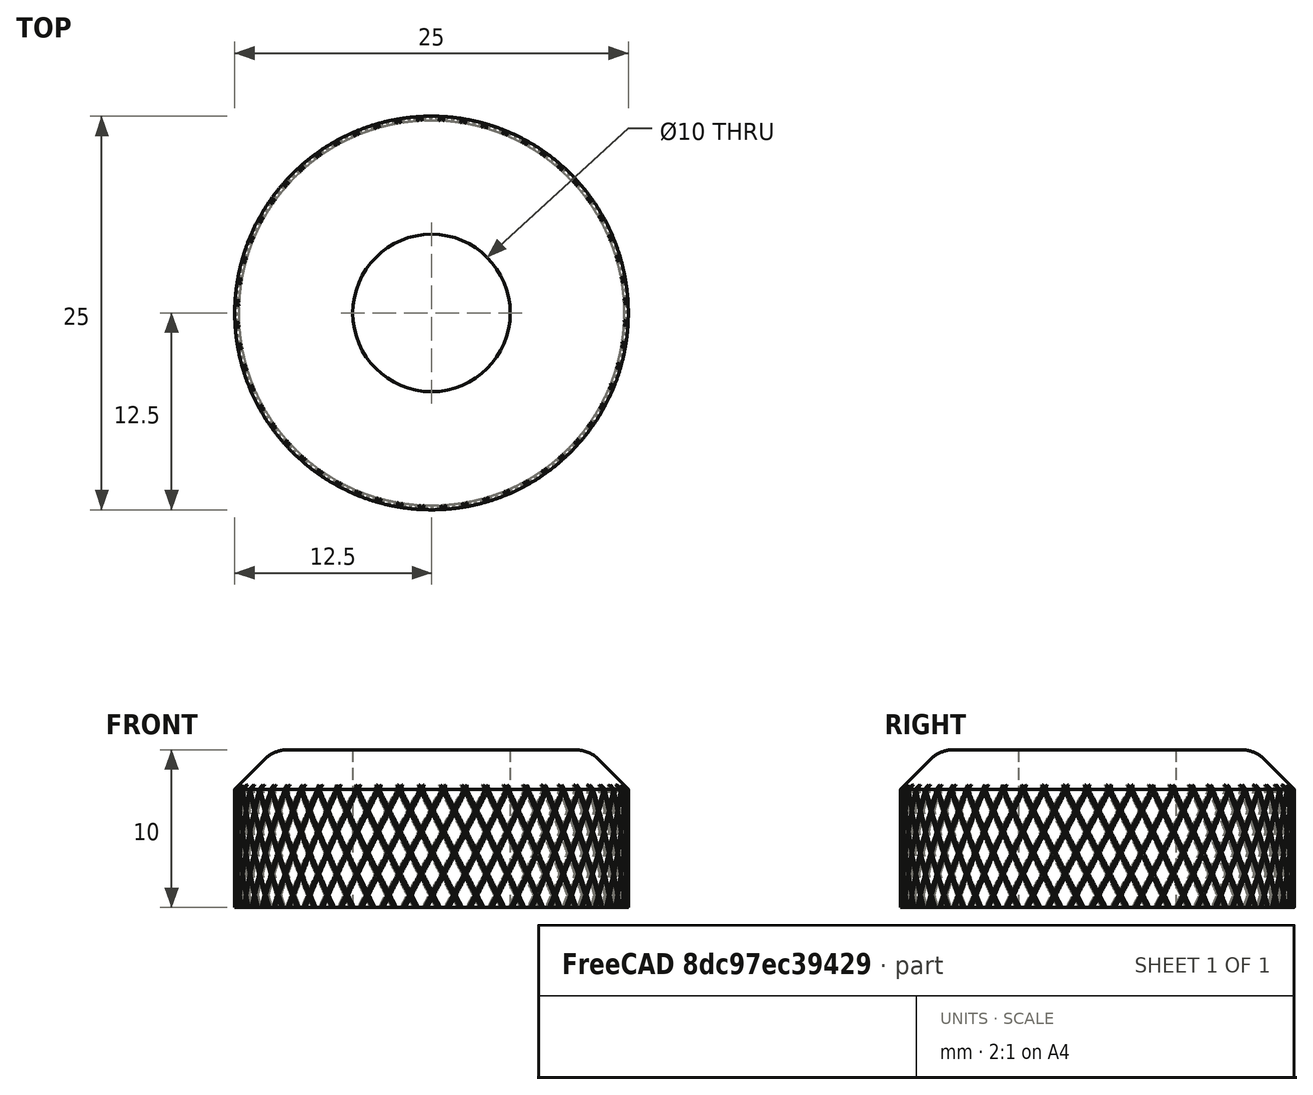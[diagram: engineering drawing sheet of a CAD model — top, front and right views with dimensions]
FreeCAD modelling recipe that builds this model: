
FCSTD DOCUMENT  (FreeCAD 1.0R39319 (Git))
Label: KnurlingModel
License: All rights reserved
LicenseURL: https://en.wikipedia.org/wiki/All_rights_reserved
objects: TechDraw::DrawViewDimension×9, Sketcher::SketchObject×3, TechDraw::DrawProjGroupItem×3, PartDesign::SubtractiveHelix×2, TechDraw::DrawViewAnnotation×2, PartDesign::Pad×1, PartDesign::Chamfer×1, PartDesign::Hole×1, PartDesign::Fillet×1, PartDesign::PolarPattern×1, PartDesign::Body×1, TechDraw::DrawSVGTemplate×1, TechDraw::DrawViewImage×1, TechDraw::DrawProjGroup×1, TechDraw::DrawViewSection×1, TechDraw::DrawPage×1
note: 38 computed .brp shape members not serialized (recipe doc carries the construction recipe); baked Part::Feature solids carry a one-line shape summary decoded from their .brp

FEATURE [Sketcher::SketchObject] Sketch
  ArcFitTolerance = 1e-06
  AttachmentSupport = -> [XY_Plane]
  FullyConstrained = true
  MakeInternals = false
  MapMode = 5
  sketch-geometry (1):
    g0: Circle CenterX=0 CenterY=0 CenterZ=0 NormalX=0 NormalY=0 NormalZ=1 AngleXU=0 Radius=12.5
  constraints (2):
    c: Diameter(g0) = 25
    c: Coincident(g0,g-1)
FEATURE [PartDesign::Pad] Pad
  Direction = (0,0,1)
  Length = 10
  Length2 = 10
  Profile = -> Sketch
  ReferenceAxis = -> Sketch [N_Axis]
  Refine = true
  Suppressed = false
  Type = 0
FEATURE [PartDesign::Chamfer] Chamfer
  Angle = 45
  Base = -> Pad [Edge3]
  BaseFeature = -> Pad
  ChamferType = 0
  FlipDirection = false
  Refine = true
  Size = 2.5
  Size2 = 1
  SupportTransform = false
  Suppressed = false
  UseAllEdges = false
FEATURE [Sketcher::SketchObject] Sketch001
  ArcFitTolerance = 1e-06
  AttachmentOffset = pos=(0,0,-2) rot=(0,0,1;0rad)
  AttachmentSupport = -> [XY_Plane]
  FullyConstrained = true
  MakeInternals = false
  MapMode = 5
  Placement = pos=(0,0,-2) rot=(0,0,1;0rad)
  sketch-geometry (3):
    g0: LineSegment StartX=-0.724874 StartY=13.9812 StartZ=0 EndX=0 EndY=12.2312 EndZ=0
    g1: LineSegment StartX=0 StartY=12.2312 StartZ=0 EndX=0.724874 EndY=13.9812 EndZ=0
    g2: ArcOfCircle CenterX=0 CenterY=0 CenterZ=0 NormalX=0 NormalY=0 NormalZ=1 AngleXU=0 Radius=14 StartAngle=1.519 EndAngle=1.6226
  constraints (9):
    c: PointOnObject(g0,g-2)
    c: Coincident(g0,g1)
    c: Angle(g1,g0) = 0.785398
    c: Coincident(g2,g-1)
    c: Coincident(g2,g1)
    c: Coincident(g2,g0)
    c: Radius(g2) = 14
    c: Horizontal(g1,g0)
    c: DistanceY(g1,g1) = 1.75
FEATURE [Sketcher::SketchObject] MirroredSketch
  ArcFitTolerance = 1e-06
  FullyConstrained = true
  MakeInternals = false
  Placement = pos=(0,0,-2) rot=(0,0,1;0.120951rad)
  sketch-geometry (3):
    g0: LineSegment StartX=-0.724874 StartY=-13.9812 StartZ=0 EndX=0 EndY=-12.2312 EndZ=0
    g1: LineSegment StartX=0 StartY=-12.2312 StartZ=0 EndX=0.724874 EndY=-13.9812 EndZ=0
    g2: ArcOfCircle CenterX=0 CenterY=0 CenterZ=0 NormalX=0 NormalY=0 NormalZ=1 AngleXU=0 Radius=14 StartAngle=4.66059 EndAngle=4.76419
  constraints (9):
    c: Coincident(g0,g1)
    c: Angle(g1,g0) = -0.785398
    c: Coincident(g2,g1)
    c: Coincident(g2,g0)
    c: Radius(g2) = 14
    c: PointOnObject(g0,g-2)
    c: Horizontal(g1,g0)
    c: DistanceY(g1,g1) = 1.75
    c: Coincident(g2,g-1)
FEATURE [PartDesign::Hole] Hole
  BaseFeature = -> Chamfer
  CustomThreadClearance = 0
  Depth = 25
  DepthType = 0
  Diameter = 10
  DrillForDepth = false
  DrillPoint = 1
  DrillPointAngle = 118
  HoleCutCountersinkAngle = 90
  HoleCutCustomValues = false
  HoleCutDepth = 0
  HoleCutDiameter = 6.1
  HoleCutType = 0
  ModelThread = false
  Profile = -> Chamfer [Face4]
  Refine = true
  Suppressed = false
  Tapered = false
  TaperedAngle = 90
  ThreadClass = 0
  ThreadDepth = 25
  ThreadDepthType = 0
  ThreadDirection = 0
  ThreadFit = 0
  ThreadSize = 0
  ThreadType = 0
  Threaded = false
  UseCustomThreadClearance = false
FEATURE [PartDesign::Fillet] Fillet
  Base = -> Hole [Edge5]
  BaseFeature = -> Hole
  Radius = 2
  Refine = true
  SupportTransform = false
  Suppressed = false
  UseAllEdges = false
FEATURE [PartDesign::SubtractiveHelix] SubtractiveHelix
  Angle = 0
  Axis = (1e-16,1e-16,1)
  Base = (0,0,0)
  BaseFeature = -> Fillet
  Growth = 0
  HasBeenEdited = true
  Height = 12
  LeftHanded = false
  Mode = 0
  Outside = false
  Pitch = 150
  Profile = -> Sketch001
  ReferenceAxis = -> Z_Axis
  Refine = true
  Suppressed = false
  Tolerance = 0.1
  Turns = 0.08
FEATURE [PartDesign::SubtractiveHelix] SubtractiveHelix001
  Angle = 0
  Axis = (1e-16,1e-16,1)
  Base = (0,0,0)
  BaseFeature = -> SubtractiveHelix
  Growth = 0
  HasBeenEdited = true
  Height = 12
  LeftHanded = true
  Mode = 0
  Outside = false
  Pitch = 150
  Profile = -> MirroredSketch
  ReferenceAxis = -> Z_Axis
  Refine = true
  Suppressed = false
  Tolerance = 0.1
  Turns = 0.08
FEATURE [PartDesign::PolarPattern] PolarPattern
  Angle = 360
  Axis = -> Sketch001 [N_Axis]
  BaseFeature = -> SubtractiveHelix001
  Mode = 0
  Occurrences = 56
  Offset = 120
  Originals = -> [SubtractiveHelix,SubtractiveHelix001]
  Refine = true
  Suppressed = false
  TransformMode = 0
FEATURE [PartDesign::Body] Body
  AllowCompound = false
  Group = -> [Sketch,Pad,Chamfer,Sketch001,MirroredSketch,Hole,Fillet,SubtractiveHelix,SubtractiveHelix001,PolarPattern]
  Origin = -> Origin
  Tip = -> PolarPattern
FEATURE [TechDraw::DrawSVGTemplate] Template
  EditableTexts = approval_person=B. Hecate; creator=KUN-YI CHEN; date_of_issue=10/25/25; document_type=Component Drawing; general_tolerances=ISO 2768-m; identification_number=DN; language_code=EN; legal_owner_1=UWINGS TECHNOLOIGES; part_material=Stainless steel Mat.No. 1.4301; revision_index=AAA; scale=1 : 1; sheet_number=1 / 1; title=Knurling Demo Model
  Height = 210
  Orientation = 1
  Template = <path>
  Width = 297
FEATURE [TechDraw::DrawViewImage] ActiveView
  Height = 72.4
  ImageFile = <userpath>/.cache/FreeCAD/Cache/FreeCAD_Doc_d9a276a7-9c46-4152-82e7-83487e9de5cd_6feaea_92105/PageActiveViewvjlq21.png
  LockPosition = false
  Rotation = 0
  Scale = 0.8
  ScaleType = 2
  Width = 72
  X = 165.05
  Y = 154.756
FEATURE [TechDraw::DrawProjGroupItem] View  label="Front"
  CoarseView = false
  Direction = (6e-16,-2e-16,-1)
  Focus = 150
  HardHidden = false
  IsoCount = 0
  IsoHidden = false
  IsoVisible = false
  LockPosition = true
  Perspective = false
  Rotation = 0
  RotationVector = (1,0,0)
  Scale = 2.66667
  ScaleType = 2
  ScrubCount = 0
  SeamHidden = false
  SeamVisible = false
  SmoothHidden = false
  SmoothVisible = true
  Source = -> [Fillet]
  Type = 0
  X = 0
  XDirection = (-1e-16,1,-2e-16)
  Y = 0
FEATURE [TechDraw::DrawProjGroupItem] ProjItem  label="Top"
  CoarseView = false
  Direction = (1,1e-16,6e-16)
  Focus = 100
  HardHidden = false
  IsoCount = 0
  IsoHidden = false
  IsoVisible = false
  LockPosition = false
  Perspective = false
  Rotation = 0
  RotationVector = (1,0,0)
  Scale = 2.66667
  ScaleType = 2
  ScrubCount = 1
  SeamHidden = false
  SeamVisible = false
  SmoothHidden = false
  SmoothVisible = true
  Source = -> [Fillet]
  Type = 4
  X = 0
  XDirection = (-1e-16,1,-2e-16)
  Y = -71.6667
FEATURE [TechDraw::DrawProjGroup] ProjGroup
  Anchor = -> View
  AutoDistribute = true
  LockPosition = false
  ProjectionType = 0
  Rotation = 0
  Scale = 2.66667
  ScaleType = 2
  Source = -> [Fillet]
  Views = -> [View,ProjItem]
  X = 74.1881
  Y = 154.756
  spacingX = 25
  spacingY = 25
FEATURE [TechDraw::DrawViewDimension] Dimension
  AngleOverride = false
  Arbitrary = false
  ArbitraryTolerances = false
  BoxCorners = (2) [(-33.3333,-33.3333,0),(33.3333,33.3333,0)]
  EqualTolerance = true
  ExtensionAngle = 0
  FormatSpec = ⌀%.2w
  FormatSpecOverTolerance = %+.2w
  FormatSpecUnderTolerance = %+.2w
  Inverted = false
  LineAngle = 0
  LockPosition = false
  MeasureType = 1
  OverTolerance = 0
  References2D = -> [View]
  Rotation = 0
  ScaleType = 0
  TheoreticalExact = false
  Type = 5
  UnderTolerance = 0
  X = 39.1122
  Y = -24.381
FEATURE [TechDraw::DrawViewSection] SectionView  label="Section A-A"
  BaseView = -> View
  CoarseView = false
  CutSurfaceDisplay = 2
  Direction = (1,4e-16,6e-16)
  FileGeomPattern = <path>
  FileHatchPattern = <path>
  Focus = 100
  FuseBeforeCut = false
  HardHidden = false
  HatchOffset = (0,0,0)
  HatchRotation = 0
  HatchScale = 1
  IsoCount = 0
  IsoHidden = false
  IsoVisible = false
  LockPosition = false
  NameGeomPattern = Diamond
  Perspective = false
  Rotation = 0
  Scale = 2.66667
  ScaleType = 2
  ScrubCount = 1
  SeamHidden = false
  SeamVisible = false
  SectionDirection = 4
  SectionLineStretch = 1
  SectionNormal = (1,4e-16,6e-16)
  SectionOrigin = (0,0,5)
  SectionSymbol = A
  SmoothHidden = false
  SmoothVisible = true
  Source = -> [Fillet]
  TrimAfterCut = false
  UsePreviousCut = false
  X = 68.9616
  XDirection = (-4e-16,1,-2e-16)
  Y = 76.6489
FEATURE [TechDraw::DrawViewDimension] Dimension001
  AngleOverride = false
  Arbitrary = false
  ArbitraryTolerances = false
  BoxCorners = (2) [(-33.3333,-13.3333,-1e-07),(33.3333,13.3333,1e-07)]
  EqualTolerance = true
  ExtensionAngle = 0
  FormatSpec = %.2w
  FormatSpecOverTolerance = %+.2w
  FormatSpecUnderTolerance = %+.2w
  Inverted = false
  LineAngle = 0
  LockPosition = false
  MeasureType = 1
  OverTolerance = 0
  References2D = -> [SectionView]
  Rotation = 0
  ScaleType = 0
  TheoreticalExact = false
  Type = 1
  UnderTolerance = 0
  X = 0
  Y = -32.2529
FEATURE [TechDraw::DrawViewDimension] Dimension002
  AngleOverride = false
  Arbitrary = false
  ArbitraryTolerances = false
  BoxCorners = (2) [(-33.3333,-13.3333,-1e-07),(33.3333,13.3333,1e-07)]
  EqualTolerance = true
  ExtensionAngle = 0
  FormatSpec = R%.2w
  FormatSpecOverTolerance = %+.2w
  FormatSpecUnderTolerance = %+.2w
  Inverted = false
  LineAngle = 0
  LockPosition = false
  MeasureType = 1
  OverTolerance = 0
  References2D = -> [SectionView]
  Rotation = 0
  ScaleType = 0
  TheoreticalExact = false
  Type = 4
  UnderTolerance = 0
  X = 27.6489
  Y = 28.5213
FEATURE [TechDraw::DrawViewDimension] Dimension003
  AngleOverride = false
  Arbitrary = false
  ArbitraryTolerances = false
  BoxCorners = (2) [(-33.3333,-13.3333,-1e-07),(33.3333,13.3333,1e-07)]
  EqualTolerance = true
  ExtensionAngle = 0
  FormatSpec = %.2w
  FormatSpecOverTolerance = %+.2w
  FormatSpecUnderTolerance = %+.2w
  Inverted = false
  LineAngle = 0
  LockPosition = false
  MeasureType = 1
  OverTolerance = 0
  References2D = -> [SectionView]
  Rotation = 0
  ScaleType = 0
  TheoreticalExact = false
  Type = 2
  UnderTolerance = 0
  X = 65.6013
  Y = -4.1905
FEATURE [TechDraw::DrawViewDimension] Dimension004
  AngleOverride = false
  Arbitrary = false
  ArbitraryTolerances = false
  BoxCorners = (2) [(-33.3333,-13.3333,-1e-07),(33.3333,13.3333,1e-07)]
  EqualTolerance = true
  ExtensionAngle = 0
  FormatSpec = %.2w
  FormatSpecOverTolerance = %+.2w
  FormatSpecUnderTolerance = %+.2w
  Inverted = false
  LineAngle = 0
  LockPosition = false
  MeasureType = 1
  OverTolerance = 0
  References2D = -> [SectionView]
  Rotation = 0
  ScaleType = 0
  TheoreticalExact = false
  Type = 6
  UnderTolerance = 0
  X = -0.336242
  Y = 28.4378
FEATURE [TechDraw::DrawViewDimension] Dimension005
  AngleOverride = false
  Arbitrary = false
  ArbitraryTolerances = false
  BoxCorners = (2) [(-33.3333,-13.3333,-1e-07),(33.3333,13.3333,1e-07)]
  EqualTolerance = true
  ExtensionAngle = 0
  FormatSpec = %.2w
  FormatSpecOverTolerance = %+.2w
  FormatSpecUnderTolerance = %+.2w
  Inverted = false
  LineAngle = 0
  LockPosition = false
  MeasureType = 1
  OverTolerance = 0
  References2D = -> [SectionView]
  Rotation = 0
  ScaleType = 0
  TheoreticalExact = false
  Type = 2
  UnderTolerance = 0
  X = 48.3444
  Y = -7.55789
FEATURE [TechDraw::DrawViewAnnotation] Annotation
  Font = osifont
  LineSpace = 100
  LockPosition = false
  MaxWidth = -1
  Rotation = 0
  ScaleType = 0
  Text = Knurling/Helix | Pitch: 150 | Height:12
  TextSize = 5
  TextStyle = 0
  X = 241.672
  Y = 160.061
FEATURE [TechDraw::DrawProjGroupItem] View001
  CoarseView = false
  Direction = (0,0,1)
  Focus = 100
  HardHidden = false
  IsoCount = 0
  IsoHidden = false
  IsoVisible = false
  LockPosition = false
  Perspective = false
  Rotation = 0
  RotationVector = (1,0,0)
  Scale = 5
  ScaleType = 2
  ScrubCount = 1
  SeamHidden = false
  SeamVisible = false
  SmoothHidden = false
  SmoothVisible = true
  Source = -> [Sketch001]
  Type = 0
  X = 218.42
  XDirection = (1,0,0)
  Y = 113.229
FEATURE [TechDraw::DrawViewDimension] Dimension006
  AngleOverride = false
  Arbitrary = false
  ArbitraryTolerances = false
  BoxCorners = (2) [(-3.62437,-4.42195,0),(3.62437,4.42195,0)]
  EqualTolerance = true
  ExtensionAngle = 0
  FormatSpec = R%.2w
  FormatSpecOverTolerance = %+.2w
  FormatSpecUnderTolerance = %+.2w
  Inverted = false
  LineAngle = 0
  LockPosition = false
  MeasureType = 1
  OverTolerance = 0
  References2D = -> [View001]
  Rotation = 0
  ScaleType = 0
  TheoreticalExact = false
  Type = 4
  UnderTolerance = 0
  X = 39.7177
  Y = -17.8998
FEATURE [TechDraw::DrawViewDimension] Dimension007
  AngleOverride = false
  Arbitrary = false
  ArbitraryTolerances = false
  BoxCorners = (2) [(-3.62437,-4.42195,0),(3.62437,4.42195,0)]
  EqualTolerance = true
  ExtensionAngle = 0
  FormatSpec = %.2w
  FormatSpecOverTolerance = %+.2w
  FormatSpecUnderTolerance = %+.2w
  Inverted = false
  LineAngle = 0
  LockPosition = false
  MeasureType = 1
  OverTolerance = 0
  References2D = -> [View001]
  Rotation = 0
  ScaleType = 0
  TheoreticalExact = false
  Type = 6
  UnderTolerance = 0
  X = -2.19548
  Y = 19.6146
FEATURE [TechDraw::DrawViewDimension] Dimension008
  AngleOverride = false
  Arbitrary = false
  ArbitraryTolerances = false
  BoxCorners = (2) [(-3.62437,-4.42195,0),(3.62437,4.42195,0)]
  EqualTolerance = true
  ExtensionAngle = 0
  FormatSpec = %.2w
  FormatSpecOverTolerance = %+.2w
  FormatSpecUnderTolerance = %+.2w
  Inverted = false
  LineAngle = 0
  LockPosition = false
  MeasureType = 1
  OverTolerance = 0
  References2D = -> [View001]
  Rotation = 0
  ScaleType = 0
  TheoreticalExact = false
  Type = 2
  UnderTolerance = 0
  X = 14.3321
  Y = 18.7476
FEATURE [TechDraw::DrawViewAnnotation] Annotation001
  Font = osifont
  LineSpace = 100
  LockPosition = false
  MaxWidth = -1
  Rotation = 0
  ScaleType = 0
  Text = 56 Ocurrents
  TextSize = 5
  TextStyle = 0
  X = 263.373
  Y = 125.413
FEATURE [TechDraw::DrawPage] Page
  KeepUpdated = true
  NextBalloonIndex = 1
  ProjectionType = 0
  Template = -> Template
  Views = -> [ActiveView,ProjGroup,Dimension,SectionView,Dimension001,Dimension002,Dimension003,Dimension004,Dimension005,Annotation,View001,Dimension006,Dimension007,Dimension008,Annotation001]
note: 3 file-system paths scrubbed to <path> (originals preserved in the JSON sidecar)
